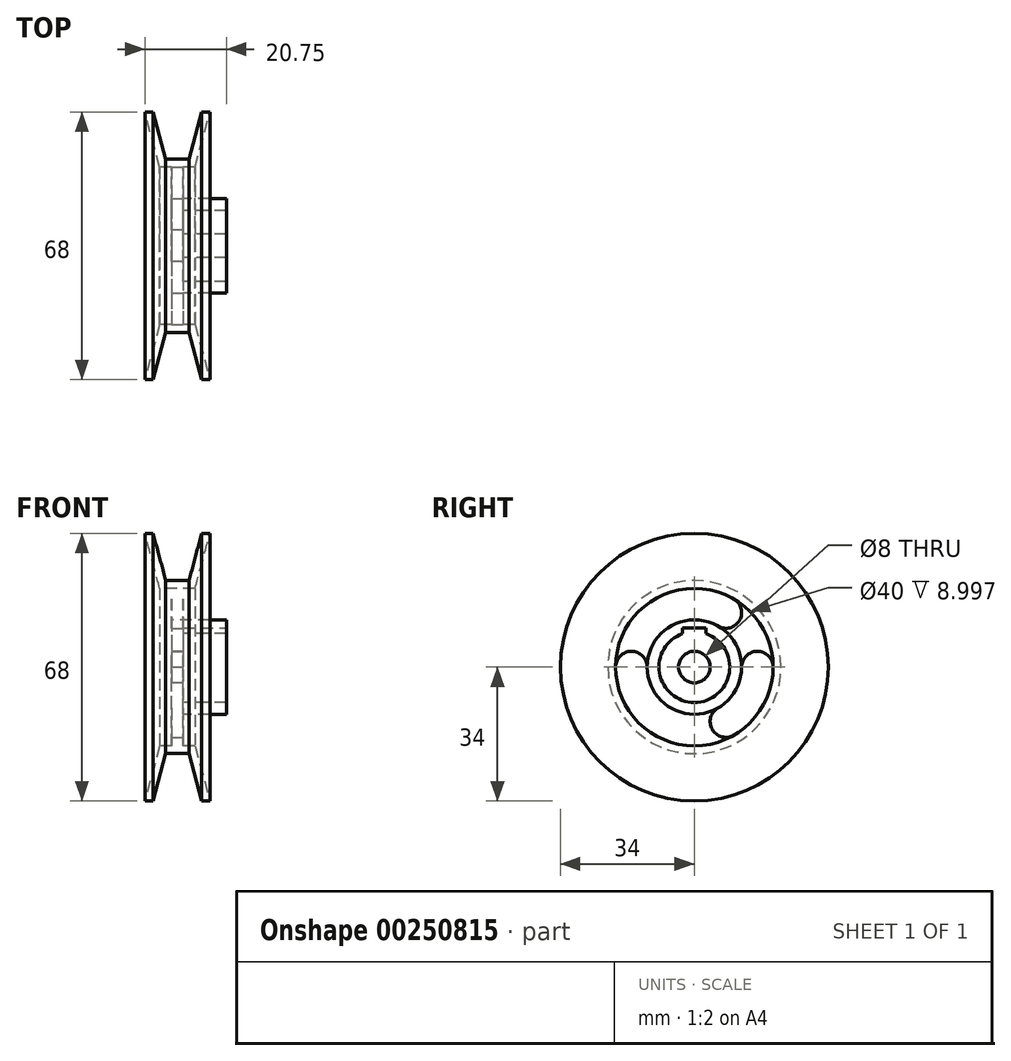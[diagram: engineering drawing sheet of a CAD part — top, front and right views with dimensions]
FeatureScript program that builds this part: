
annotation { "Feature Type Name" : "Feature", "Feature Type Description" : "" }
export const myFeature = defineFeature(function(context is Context, id is Id, definition is map)
    precondition{}
    {
        {
            var Q0;
            Q0=qCreatedBy(makeId("Front.planeOp"),FACE);
            var sketch = newSketch(context, id + "F0", { "sketchPlane" : qUnion([Q0])});
            skLineSegment(sketch, "E0", {"start": v(6.18, 34) * mm, "end": v(8.25, 34) * mm});
            skLineSegment(sketch, "E1", {"start": v(6.18, 34) * mm, "end": v(2.96, 22) * mm});
            skLineSegment(sketch, "E2", {"start": v(8.25, 34) * mm, "end": v(4.5, 20) * mm});
            skLineSegment(sketch, "E3", {"start": v(2.96, 22) * mm, "end": v(0, 22) * mm});
            skLineSegment(sketch, "E4", {"start": v(4.5, 20) * mm, "end": v(1.5, 20) * mm});
            skLineSegment(sketch, "E5", {"start": v(1.5, 20) * mm, "end": v(1.5, 12) * mm});
            skLineSegment(sketch, "E6.MirrorCS", {"start": v(-4.5, 20) * mm, "end": v(-1.5, 20) * mm});
            skLineSegment(sketch, "E7.MirrorCS", {"start": v(-1.5, 20) * mm, "end": v(-1.5, 4) * mm});
            skLineSegment(sketch, "E8.MirrorCS", {"start": v(-8.25, 34) * mm, "end": v(-4.5, 20) * mm});
            skLineSegment(sketch, "E9.MirrorCS", {"start": v(-6.18, 34) * mm, "end": v(-2.96, 22) * mm});
            skLineSegment(sketch, "E10.MirrorCS", {"start": v(-6.18, 34) * mm, "end": v(-8.25, 34) * mm});
            skLineSegment(sketch, "E11.MirrorCS", {"start": v(-2.96, 22) * mm, "end": v(0, 22) * mm});
            skLineSegment(sketch, "E12", {"start": v(-1.5, 4) * mm, "end": v(1.5, 4) * mm});
            skLineSegment(sketch, "E13", {"start": v(-22.44, 0) * mm, "end": v(29.6, 0) * mm, "construction": true});
            skLineSegment(sketch, "E14", {"start": v(1.5, 12) * mm, "end": v(12.5, 12) * mm});
            skLineSegment(sketch, "E15", {"start": v(12.5, 12) * mm, "end": v(12.5, 9) * mm});
            skLineSegment(sketch, "E16", {"start": v(12.5, 9) * mm, "end": v(1.5, 9) * mm});
            skLineSegment(sketch, "E17.trimOffspring", {"start": v(1.5, 9) * mm, "end": v(1.5, 4) * mm});
            skSolve(sketch);
        }
        {
            var Q0;
            Q0 = qSketchRegion(id + "F0", true);
            var Q1;
            Q1=sQuery(id+"F0.wireOp",EDGE,"E13");
            revolve(context, id + "F1", {"surfaceOperationType" : NewSurfaceOperationType.NEW, "entities" : qUnion([Q0]), "axis" : qUnion([Q1]), "revolveType" : RevolveType.FULL});
        }
        {
            var Q0;
            Q0=makeQuery(id+"F1.opRevolve","SWEPT_FACE",FACE,{"disambiguationData":[OSD([sQuery(id+"F0.wireOp",EDGE,"E15")])]});
            var sketch = newSketch(context, id + "F2", { "sketchPlane" : qUnion([Q0])});
            skLineSegment(sketch, "E18.bottom", {"start": v(3, 10) * mm, "end": v(-3, 10) * mm});
            skLineSegment(sketch, "E18.top", {"start": v(3, 8) * mm, "end": v(-3, 8) * mm});
            skLineSegment(sketch, "E18.left", {"start": v(3, 10) * mm, "end": v(3, 8) * mm});
            skLineSegment(sketch, "E18.right", {"start": v(-3, 10) * mm, "end": v(-3, 8) * mm});
            skPoint(sketch, "E18.middle", {"position": v(0, 9) * mm});
            skSolve(sketch);
        }
        {
            var Q0;
            Q0 = qSketchRegion(id + "F2", true);
            extrude(context, id + "F3", {"entities" : qUnion([Q0]), "operationType" : NewBodyOperationType.REMOVE, "oppositeDirection" : true, "depth" : 11 * mm, "offsetDistance" : 25 * mm});
        }
        {
            var Q0;
            Q0=makeQuery(id+"F1.opRevolve","SWEPT_FACE",FACE,{"disambiguationData":[OSD([sQuery(id+"F0.wireOp",EDGE,"E5")])]});
            var sketch = newSketch(context, id + "F4", { "sketchPlane" : qUnion([Q0])});
            skArc(sketch, "E19", {"start": v(-16, 0) * mm, "mid": v(-13.86, -8) * mm, "end": v(-8, -13.86) * mm});
            skLineSegment(sketch, "E20", {"start": v(-8, -13.86) * mm, "end": v(0, 0) * mm, "construction": true});
            skArc(sketch, "E21.0.startCap", {"start": v(-20, 0) * mm, "mid": v(-16, 4) * mm, "end": v(-12, 0) * mm});
            skArc(sketch, "E21.0.endCap", {"start": v(-6, -10.4) * mm, "mid": v(-4.54, -15.86) * mm, "end": v(-10, -17.32) * mm});
            skArc(sketch, "E21.0.left", {"start": v(-12, 0) * mm, "mid": v(-10.4, -6) * mm, "end": v(-6, -10.4) * mm});
            skArc(sketch, "E21.0.right", {"start": v(-20, 0) * mm, "mid": v(-17.32, -10) * mm, "end": v(-10, -17.32) * mm});
            skArc(sketch, "E22.1.0", {"start": v(8, -13.86) * mm, "mid": v(13.86, -8) * mm, "end": v(16, 0) * mm});
            skArc(sketch, "E22.1.1", {"start": v(10, -17.32) * mm, "mid": v(17.32, -10) * mm, "end": v(20, 0) * mm});
            skArc(sketch, "E22.1.2", {"start": v(6, -10.4) * mm, "mid": v(10.4, -6) * mm, "end": v(12, 0) * mm});
            skArc(sketch, "E22.1.3", {"start": v(12, 0) * mm, "mid": v(16, 4) * mm, "end": v(20, 0) * mm});
            skArc(sketch, "E22.1.4", {"start": v(10, -17.32) * mm, "mid": v(4.54, -15.86) * mm, "end": v(6, -10.4) * mm});
            skArc(sketch, "E22.2.0", {"start": v(8, 13.86) * mm, "mid": v(0, 16) * mm, "end": v(-8, 13.86) * mm});
            skArc(sketch, "E22.2.1", {"start": v(10, 17.32) * mm, "mid": v(0, 20) * mm, "end": v(-10, 17.32) * mm});
            skArc(sketch, "E22.2.2", {"start": v(6, 10.4) * mm, "mid": v(0, 12) * mm, "end": v(-6, 10.4) * mm});
            skArc(sketch, "E22.2.3", {"start": v(-6, 10.4) * mm, "mid": v(-11.46, 11.86) * mm, "end": v(-10, 17.32) * mm});
            skArc(sketch, "E22.2.4", {"start": v(10, 17.32) * mm, "mid": v(11.46, 11.86) * mm, "end": v(6, 10.4) * mm});
            skSolve(sketch);
        }
        {
            var Q0;
            Q0=makeQuery(id+"F4.imprint","IMPRINT",FACE,{"disambiguationData":[TD([[makeQuery(id+"F4.imprint","IMPRINT",EDGE,{"derivedFrom":sQuery(id+"F4.wireOp",EDGE,"E21.0.startCap")}),-1.0]])]});
            var Q1;
            Q1=makeQuery(id+"F4.imprint","IMPRINT",FACE,{"disambiguationData":[TD([[makeQuery(id+"F4.imprint","IMPRINT",EDGE,{"derivedFrom":sQuery(id+"F4.wireOp",EDGE,"E22.2.1")}),-1.0]])]});
            var Q2;
            Q2=makeQuery(id+"F4.imprint","IMPRINT",FACE,{"disambiguationData":[TD([[makeQuery(id+"F4.imprint","IMPRINT",EDGE,{"derivedFrom":sQuery(id+"F4.wireOp",EDGE,"E22.1.1")}),-1.0]])]});
            extrude(context, id + "F5", {"entities" : qUnion([Q0, Q1, Q2]), "operationType" : NewBodyOperationType.REMOVE, "oppositeDirection" : true, "depth" : 25 * mm, "offsetDistance" : 25 * mm});
        }
    });
